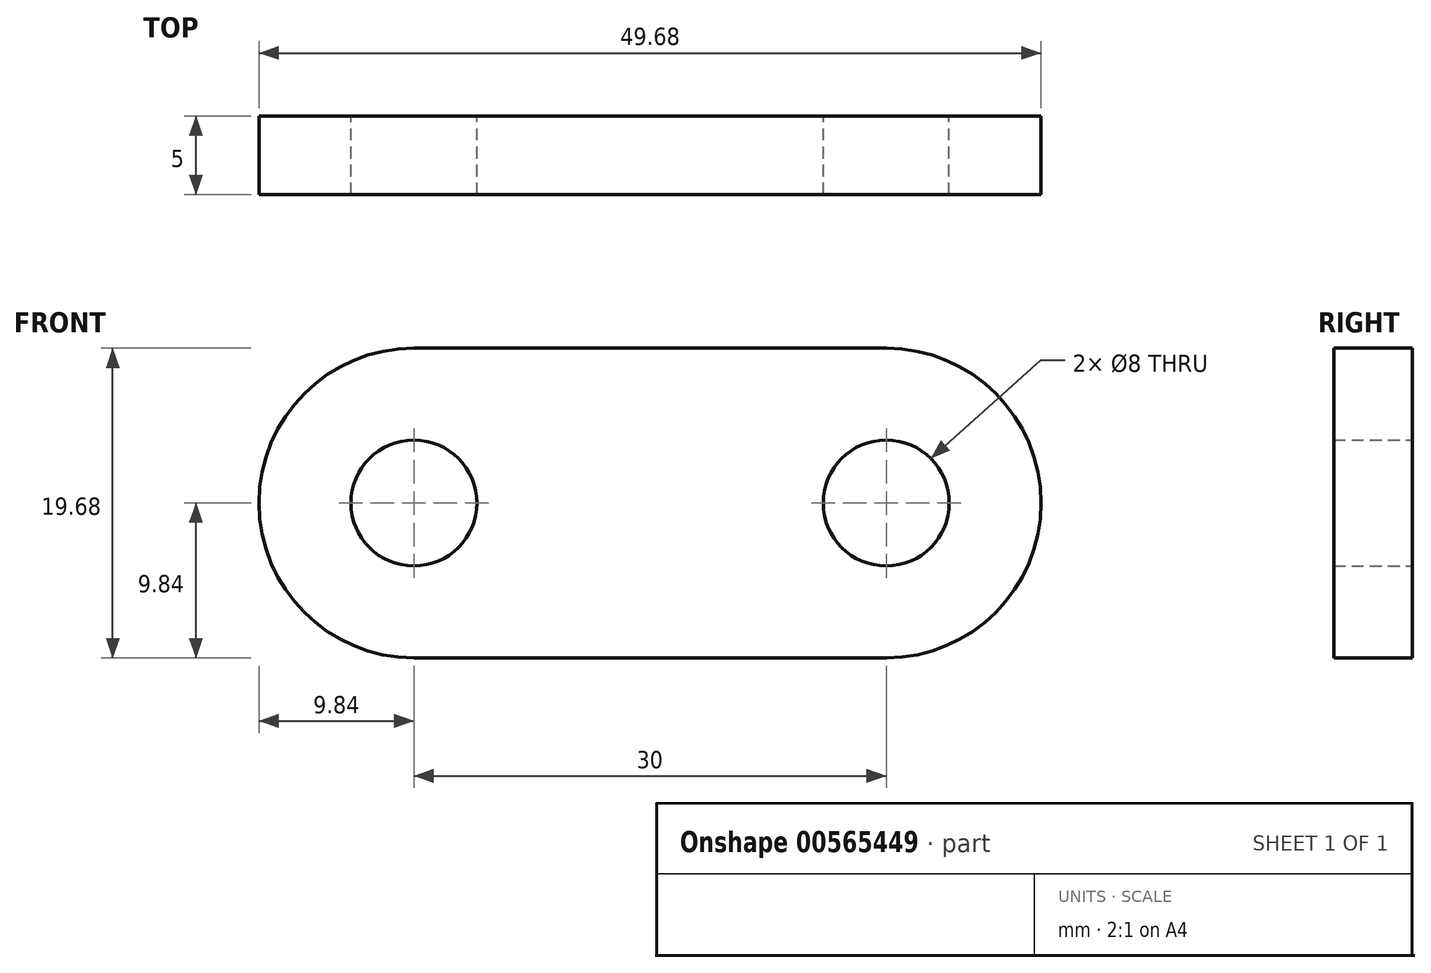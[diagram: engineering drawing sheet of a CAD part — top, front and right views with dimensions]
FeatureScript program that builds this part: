
annotation { "Feature Type Name" : "Feature", "Feature Type Description" : "" }
export const myFeature = defineFeature(function(context is Context, id is Id, definition is map)
    precondition{}
    {
        {
            var Q0;
            Q0=qCreatedBy(makeId("Front.planeOp"),FACE);
            var sketch = newSketch(context, id + "F0", { "sketchPlane" : qUnion([Q0])});
            skArc(sketch, "E0", {"start": v(-15, 9.84) * mm, "mid": v(-24.84, 0) * mm, "end": v(-15, -9.84) * mm});
            skLineSegment(sketch, "E1", {"start": v(-15, 9.84) * mm, "end": v(0, 9.84) * mm});
            skLineSegment(sketch, "E2", {"start": v(-15, -9.84) * mm, "end": v(0, -9.83) * mm});
            skLineSegment(sketch, "E3.MirrorCS", {"start": v(15, 9.84) * mm, "end": v(0, 9.84) * mm});
            skArc(sketch, "E4.MirrorCS", {"start": v(15, 9.84) * mm, "mid": v(24.84, 0) * mm, "end": v(15, -9.84) * mm});
            skLineSegment(sketch, "E5.MirrorCS", {"start": v(15, -9.84) * mm, "end": v(0, -9.83) * mm});
            skCircle(sketch, "E6", {"center": v(-15, 0) * mm, "radius": 4 * mm});
            skCircle(sketch, "E7", {"center": v(15, 0) * mm, "radius": 4 * mm});
            skSolve(sketch);
        }
        {
            var Q0;
            Q0 = qSketchRegion(id + "F0", true);
            extrude(context, id + "F1", {"entities" : qUnion([Q0]), "endBound" : BoundingType.SYMMETRIC, "depth" : 5 * mm, "offsetDistance" : 25.4 * mm});
        }
    });
